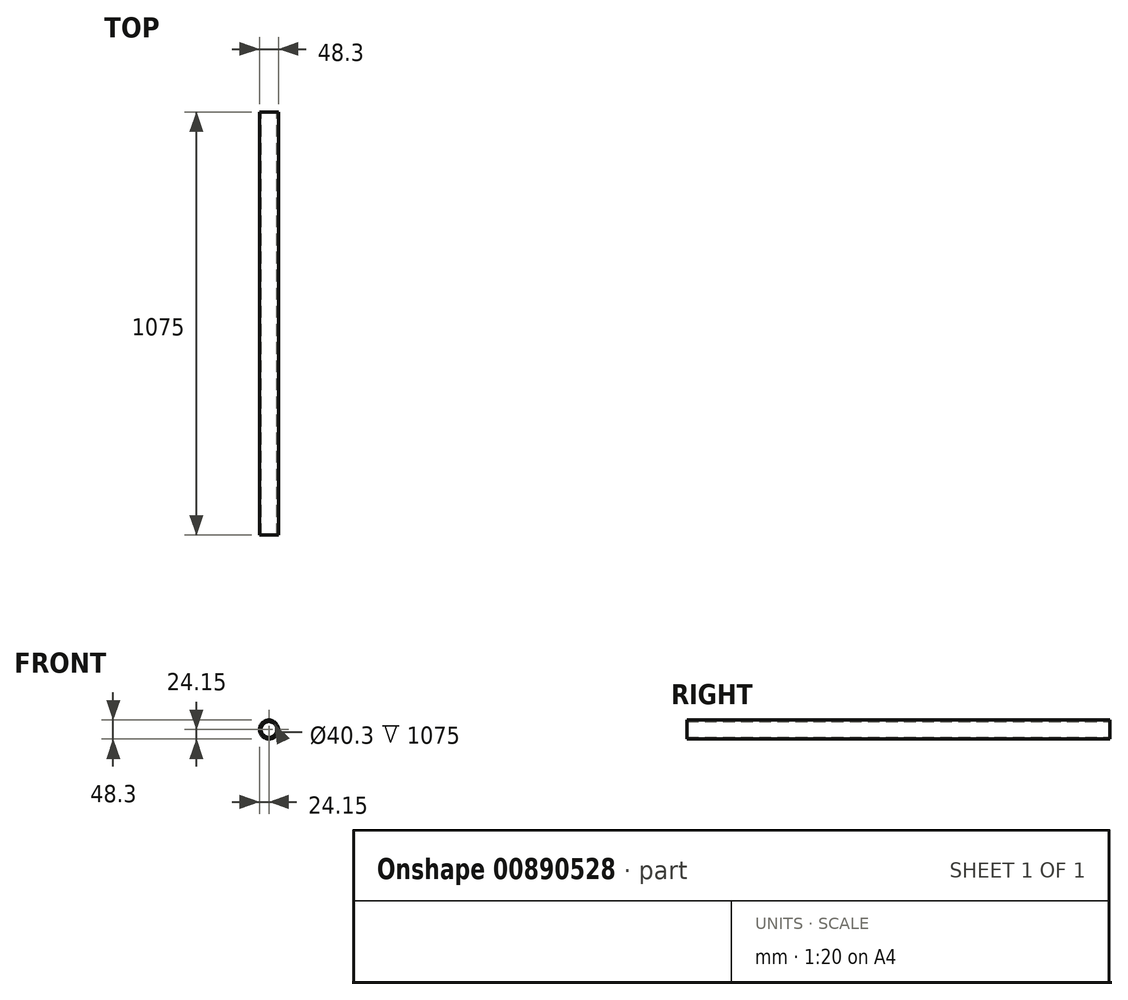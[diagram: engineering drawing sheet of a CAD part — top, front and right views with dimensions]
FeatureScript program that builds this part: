
annotation { "Feature Type Name" : "Feature", "Feature Type Description" : "" }
export const myFeature = defineFeature(function(context is Context, id is Id, definition is map)
    precondition{}
    {
        {
            var Q0;
            Q0=qCreatedBy(makeId("Front.planeOp"),FACE);
            var sketch = newSketch(context, id + "F0", { "sketchPlane" : qUnion([Q0])});
            skCircle(sketch, "E0", {"center": v(0, 0) * mm, "radius": 24.15 * mm});
            skLineSegment(sketch, "E1", {"start": v(0, -24.15) * mm, "end": v(0, -20.15) * mm});
            skCircle(sketch, "E2", {"center": v(0, 0) * mm, "radius": 20.15 * mm});
            skSolve(sketch);
        }
        {
            var Q0;
            Q0=makeQuery(id+"F0.imprint","IMPRINT",FACE,{"disambiguationData":[TD([[makeQuery(id+"F0.imprint","IMPRINT",EDGE,{"derivedFrom":sQuery(id+"F0.wireOp",EDGE,"E0")}),1.0]])]});
            extrude(context, id + "F1", {"entities" : qUnion([Q0]), "depth" : 25 * mm, "offsetDistance" : 25 * mm});
        }
        {
            var Q0;
            Q0=makeQuery(id+"F1.opExtrude","CAP_FACE",FACE,{"disambiguationData":[OSD([sQuery(id+"F0.wireOp",EDGE,"E0"),sQuery(id+"F0.wireOp",EDGE,"E2")])],"isStart":true});
            extrude(context, id + "F2", {"entities" : qUnion([Q0]), "operationType" : NewBodyOperationType.ADD, "depth" : 50 * mm, "offsetDistance" : 25 * mm});
        }
        {
            var Q0;
            Q0=makeQuery(id+"F2.opExtrude","CAP_FACE",FACE,{"disambiguationData":[OSD([sQuery(id+"F0.wireOp",EDGE,"E0"),sQuery(id+"F0.wireOp",EDGE,"E2")])],"isStart":false});
            extrude(context, id + "F3", {"entities" : qUnion([Q0]), "operationType" : NewBodyOperationType.ADD, "depth" : 1000 * mm, "offsetDistance" : 25 * mm});
        }
    });
